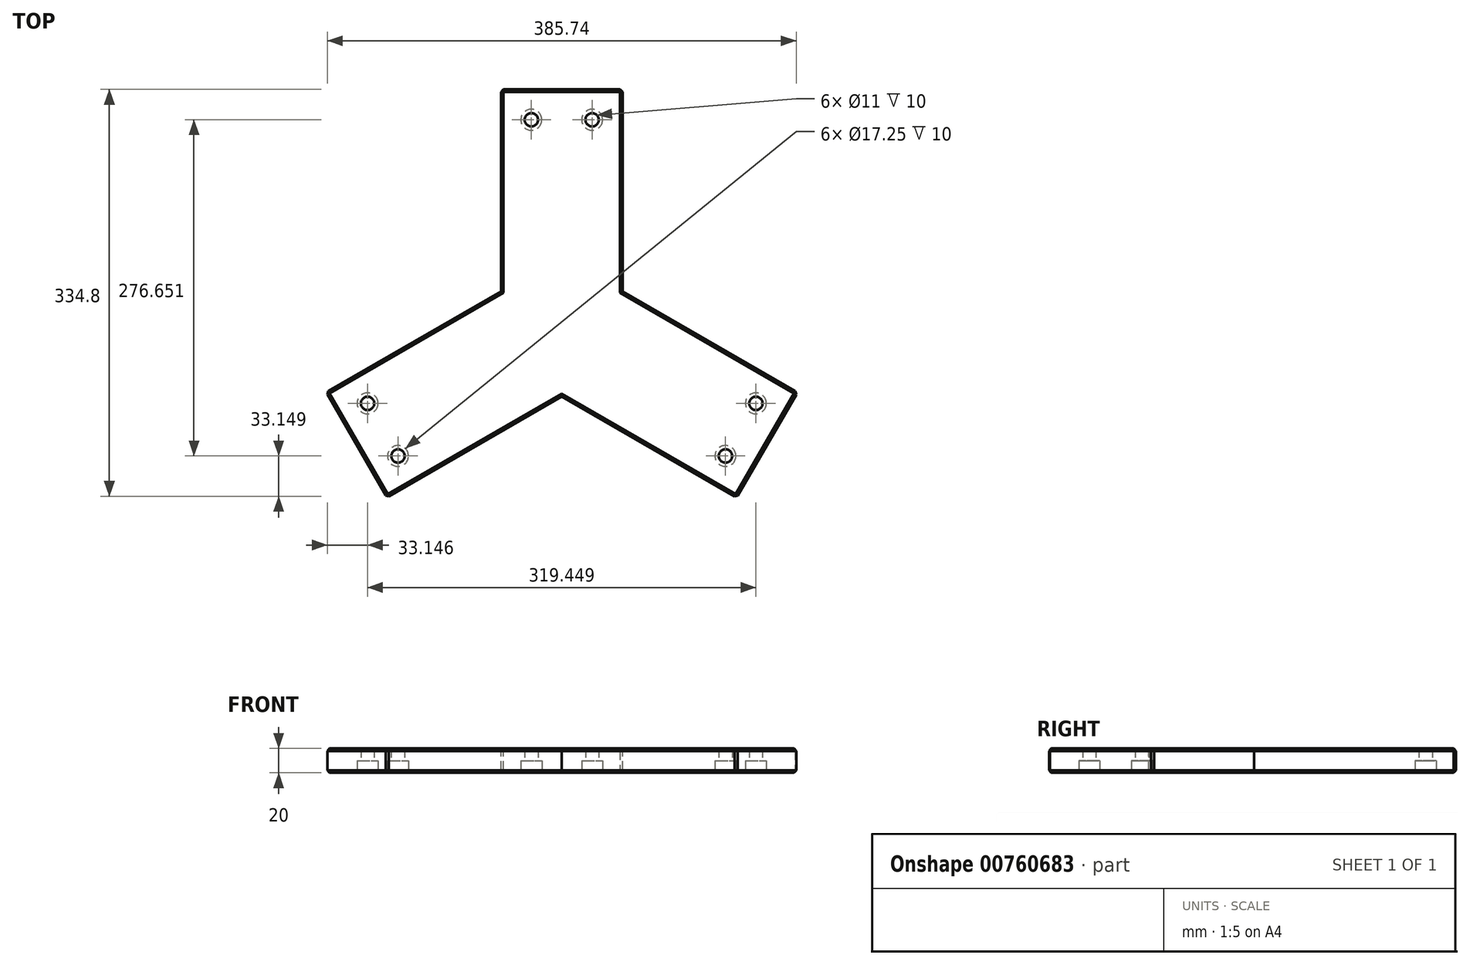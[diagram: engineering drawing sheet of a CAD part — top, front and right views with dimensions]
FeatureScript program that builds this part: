
annotation { "Feature Type Name" : "Feature", "Feature Type Description" : "" }
export const myFeature = defineFeature(function(context is Context, id is Id, definition is map)
    precondition{}
    {
        {
            var Q0;
            Q0=qCreatedBy(makeId("Top.planeOp"),FACE);
            var sketch = newSketch(context, id + "F0", { "sketchPlane" : qUnion([Q0])});
            skLineSegment(sketch, "E0.bottom", {"start": v(-50, 195) * mm, "end": v(50, 195) * mm});
            skLineSegment(sketch, "E0.left", {"start": v(-50, 28.87) * mm, "end": v(-50, 195) * mm});
            skLineSegment(sketch, "E0.right", {"start": v(50, 28.87) * mm, "end": v(50, 195) * mm});
            skLineSegment(sketch, "E1.1.0", {"start": v(0, -57.74) * mm, "end": v(-143.87, -140.8) * mm});
            skLineSegment(sketch, "E1.1.1", {"start": v(-50, 28.87) * mm, "end": v(-193.87, -54.2) * mm});
            skLineSegment(sketch, "E1.1.2", {"start": v(-143.87, -140.8) * mm, "end": v(-193.87, -54.2) * mm});
            skLineSegment(sketch, "E1.2.0", {"start": v(50, 28.87) * mm, "end": v(193.87, -54.2) * mm});
            skLineSegment(sketch, "E1.2.1", {"start": v(0, -57.74) * mm, "end": v(143.87, -140.8) * mm});
            skLineSegment(sketch, "E1.2.2", {"start": v(193.87, -54.2) * mm, "end": v(143.87, -140.8) * mm});
            skPoint(sketch, "E1.center", {"position": v(0, 0) * mm});
            skPoint(sketch, "E2.orphan", {"position": v(-114.6, 123.9) * mm});
            skPoint(sketch, "E3.orphan", {"position": v(-160.65, 35.02) * mm});
            skPoint(sketch, "E4.orphan", {"position": v(110.65, 121.62) * mm});
            skPoint(sketch, "E5.orphan", {"position": v(164.6, 37.3) * mm});
            skPoint(sketch, "E6.orphan", {"position": v(50, -156.64) * mm});
            skPoint(sketch, "E7.orphan", {"position": v(-50, -161.2) * mm});
            skSolve(sketch);
        }
        {
            var Q0;
            Q0=qSketchRegion(id+"F0",true);
            var Q1;
            Q1=makeQuery(id+"FGyLnvsjbMspBte_0.opExtrude","CAP_FACE",FACE,{"disambiguationData":[OSD([sQuery(id+"Fk0wAbcnmArPxhw_0.wireOp",EDGE,"FKqyNsek-PwpT-ekpE-xEDg-rxfoYZNdWnaj"),sQuery(id+"Fk0wAbcnmArPxhw_0.wireOp",EDGE,"oc1VOINK-Ly88-xXH5-maTl-KuvA2bRrw0Cs"),sQuery(id+"Fk0wAbcnmArPxhw_0.wireOp",EDGE,"NSF5jsu1-TvCZ-CBlY-1yNP-cmNyMix1EjlM"),sQuery(id+"Fk0wAbcnmArPxhw_0.wireOp",EDGE,"f9f7234d-7540-4040-9e6b-f4d10f7844a1.0"),sQuery(id+"Fk0wAbcnmArPxhw_0.wireOp",EDGE,"f9f7234d-7540-4040-9e6b-f4d10f7844a1.1"),sQuery(id+"Fk0wAbcnmArPxhw_0.wireOp",EDGE,"f9f7234d-7540-4040-9e6b-f4d10f7844a1.2")])],"isStart":false});
            extrude(context, id + "F1", {"entities" : qUnion([Q0]), "oppositeDirection" : true, "depth" : 20 * mm, "endBoundEntityFace" : qUnion([Q1]), "offsetDistance" : 25 * mm});
        }
        {
            var Q0;
            Q0=makeQuery(id+"F1.opExtrude","CAP_FACE",FACE,{"disambiguationData":[OSD([sQuery(id+"F0.wireOp",EDGE,"E0.bottom"),sQuery(id+"F0.wireOp",EDGE,"E0.left"),sQuery(id+"F0.wireOp",EDGE,"E0.right"),sQuery(id+"F0.wireOp",EDGE,"E1.1.0"),sQuery(id+"F0.wireOp",EDGE,"E1.1.1"),sQuery(id+"F0.wireOp",EDGE,"E1.1.2"),sQuery(id+"F0.wireOp",EDGE,"E1.2.0"),sQuery(id+"F0.wireOp",EDGE,"E1.2.1"),sQuery(id+"F0.wireOp",EDGE,"E1.2.2")])],"isStart":true});
            var Q1;
            Q1=makeQuery(id+"F1.opExtrude","CAP_FACE",FACE,{"disambiguationData":[OSD([sQuery(id+"F0.wireOp",EDGE,"E0.bottom"),sQuery(id+"F0.wireOp",EDGE,"E0.left"),sQuery(id+"F0.wireOp",EDGE,"E0.right"),sQuery(id+"F0.wireOp",EDGE,"E1.1.0"),sQuery(id+"F0.wireOp",EDGE,"E1.1.1"),sQuery(id+"F0.wireOp",EDGE,"E1.1.2"),sQuery(id+"F0.wireOp",EDGE,"E1.2.0"),sQuery(id+"F0.wireOp",EDGE,"E1.2.1"),sQuery(id+"F0.wireOp",EDGE,"E1.2.2")])],"isStart":false});
            var Q2;
            Q2=makeQuery(id+"F1.opExtrude","SWEPT_EDGE",EDGE,{"disambiguationData":[OSD([sQuery(id+"F0.wireOp",EDGE,"E1.1.0"),sQuery(id+"F0.wireOp",EDGE,"E1.1.2")])]});
            var Q3;
            Q3=makeQuery(id+"F1.opExtrude","SWEPT_EDGE",EDGE,{"disambiguationData":[OSD([sQuery(id+"F0.wireOp",EDGE,"E1.1.1"),sQuery(id+"F0.wireOp",EDGE,"E1.1.2")])]});
            var Q4;
            Q4=makeQuery(id+"F1.opExtrude","SWEPT_EDGE",EDGE,{"disambiguationData":[OSD([sQuery(id+"F0.wireOp",EDGE,"E0.bottom"),sQuery(id+"F0.wireOp",EDGE,"E0.left")])]});
            var Q5;
            Q5=makeQuery(id+"F1.opExtrude","SWEPT_EDGE",EDGE,{"disambiguationData":[OSD([sQuery(id+"F0.wireOp",EDGE,"E0.bottom"),sQuery(id+"F0.wireOp",EDGE,"E0.right")])]});
            var Q6;
            Q6=makeQuery(id+"F1.opExtrude","SWEPT_EDGE",EDGE,{"disambiguationData":[OSD([sQuery(id+"F0.wireOp",EDGE,"E1.2.0"),sQuery(id+"F0.wireOp",EDGE,"E1.2.2")])]});
            var Q7;
            Q7=makeQuery(id+"F1.opExtrude","SWEPT_EDGE",EDGE,{"disambiguationData":[OSD([sQuery(id+"F0.wireOp",EDGE,"E1.2.1"),sQuery(id+"F0.wireOp",EDGE,"E1.2.2")])]});
            chamfer(context, id + "F2", {"entities" : qUnion([Q0, Q1, Q2, Q3, Q4, Q5, Q6, Q7]), "width" : 2 * mm, "tangentPropagation" : true});
        }
        {
            var Q0;
            Q0=makeQuery(id+"F1.opExtrude","CAP_FACE",FACE,{"disambiguationData":[OSD([sQuery(id+"F0.wireOp",EDGE,"E0.bottom"),sQuery(id+"F0.wireOp",EDGE,"E0.left"),sQuery(id+"F0.wireOp",EDGE,"E0.right"),sQuery(id+"F0.wireOp",EDGE,"E1.1.0"),sQuery(id+"F0.wireOp",EDGE,"E1.1.1"),sQuery(id+"F0.wireOp",EDGE,"E1.1.2"),sQuery(id+"F0.wireOp",EDGE,"E1.2.0"),sQuery(id+"F0.wireOp",EDGE,"E1.2.1"),sQuery(id+"F0.wireOp",EDGE,"E1.2.2")])],"isStart":false});
            var sketch = newSketch(context, id + "F3", { "sketchPlane" : qUnion([Q0])});
            skPoint(sketch, "E8", {"position": v(-25, -170) * mm});
            skPoint(sketch, "E9", {"position": v(25, -170) * mm});
            skLineSegment(sketch, "E10", {"start": v(52.23, -170) * mm, "end": v(-46.28, -170) * mm, "construction": true});
            skLineSegment(sketch, "E11.1.0", {"start": v(121.1, 130.23) * mm, "end": v(170.36, 44.92) * mm, "construction": true});
            skPoint(sketch, "E11.1.1", {"position": v(159.72, 63.35) * mm});
            skPoint(sketch, "E11.1.2", {"position": v(134.72, 106.65) * mm});
            skLineSegment(sketch, "E11.2.0", {"start": v(-173.34, 39.77) * mm, "end": v(-124.09, 125.08) * mm, "construction": true});
            skPoint(sketch, "E11.2.1", {"position": v(-134.72, 106.65) * mm});
            skPoint(sketch, "E11.2.2", {"position": v(-159.72, 63.35) * mm});
            skPoint(sketch, "E11.center", {"position": v(0, 0) * mm});
            skSolve(sketch);
        }
        {
            var Q0;
            Q0=sQuery(id+"F3.wireOp",VERTEX,"E11.1.1");
            var Q1;
            Q1=sQuery(id+"F3.wireOp",VERTEX,"E11.1.2");
            var Q2;
            Q2=sQuery(id+"F3.wireOp",VERTEX,"E8");
            var Q3;
            Q3=sQuery(id+"F3.wireOp",VERTEX,"E9");
            var Q4;
            Q4=sQuery(id+"F3.wireOp",VERTEX,"E11.2.1");
            var Q5;
            Q5=sQuery(id+"F3.wireOp",VERTEX,"E11.2.2");
            var Q6;
            Q6=makeQuery(id+"F1.opExtrude","SWEPT_BODY",BODY,{"disambiguationData":[OSD([sQuery(id+"F0.wireOp",EDGE,"E0.bottom"),sQuery(id+"F0.wireOp",EDGE,"E0.left"),sQuery(id+"F0.wireOp",EDGE,"E0.right"),sQuery(id+"F0.wireOp",EDGE,"E1.1.0"),sQuery(id+"F0.wireOp",EDGE,"E1.1.1"),sQuery(id+"F0.wireOp",EDGE,"E1.1.2"),sQuery(id+"F0.wireOp",EDGE,"E1.2.0"),sQuery(id+"F0.wireOp",EDGE,"E1.2.1"),sQuery(id+"F0.wireOp",EDGE,"E1.2.2")])]});
            hole(context, id + "F4", {"style" : HoleStyle.C_BORE, "endStyle" : HoleEndStyle.THROUGH, "standardTappedOrClearance" : lookupTablePath({ "standard" : "ISO", "fit" : "Normal", "size" : "M10", "type" : "Clearance" }), "standardBlindInLast" : lookupTablePath({ "fit" : "Standard", "standard" : "ISO", "size" : "M10", "type" : "Clearance" }), "holeDiameter" : 11 * mm, "cBoreDiameter" : 17.25 * mm, "cBoreDepth" : 10 * mm, "majorDiameter" : 5 * mm, "isTappedThrough" : true, "tappedDepth" : 12 * mm, "tapClearance" : 3, "locations" : qUnion([Q0, Q1, Q2, Q3, Q4, Q5]), "scope" : qUnion([Q6])});
        }
        {
            var Q0;
            Q0=makeQuery(id+"F1.opExtrude","SWEPT_BODY",BODY,{"disambiguationData":[OSD([sQuery(id+"F0.wireOp",EDGE,"E0.bottom"),sQuery(id+"F0.wireOp",EDGE,"E0.left"),sQuery(id+"F0.wireOp",EDGE,"E0.right"),sQuery(id+"F0.wireOp",EDGE,"E1.1.0"),sQuery(id+"F0.wireOp",EDGE,"E1.1.1"),sQuery(id+"F0.wireOp",EDGE,"E1.1.2"),sQuery(id+"F0.wireOp",EDGE,"E1.2.0"),sQuery(id+"F0.wireOp",EDGE,"E1.2.1"),sQuery(id+"F0.wireOp",EDGE,"E1.2.2")])]});
            transform(context, id + "F5", {"entities" : qUnion([Q0]), "transformType" : TransformType.TRANSLATION_3D, "dx" : 0 * mm, "dy" : 0 * mm, "dz" : 0 * mm, "makeCopy" : true});
        }
        {
            var Q0;
            Q0=makeQuery(id+"F5.opPattern","COPY",BODY,{"derivedFrom":makeQuery(id+"F1.opExtrude","SWEPT_BODY",BODY,{"disambiguationData":[OSD([sQuery(id+"F0.wireOp",EDGE,"E0.bottom"),sQuery(id+"F0.wireOp",EDGE,"E0.left"),sQuery(id+"F0.wireOp",EDGE,"E0.right"),sQuery(id+"F0.wireOp",EDGE,"E1.1.0"),sQuery(id+"F0.wireOp",EDGE,"E1.1.1"),sQuery(id+"F0.wireOp",EDGE,"E1.1.2"),sQuery(id+"F0.wireOp",EDGE,"E1.2.0"),sQuery(id+"F0.wireOp",EDGE,"E1.2.1"),sQuery(id+"F0.wireOp",EDGE,"E1.2.2")])]}),"instanceName":"1"});
            deleteBodies(context, id + "F6", {"entities" : qUnion([Q0])});
        }
    });
